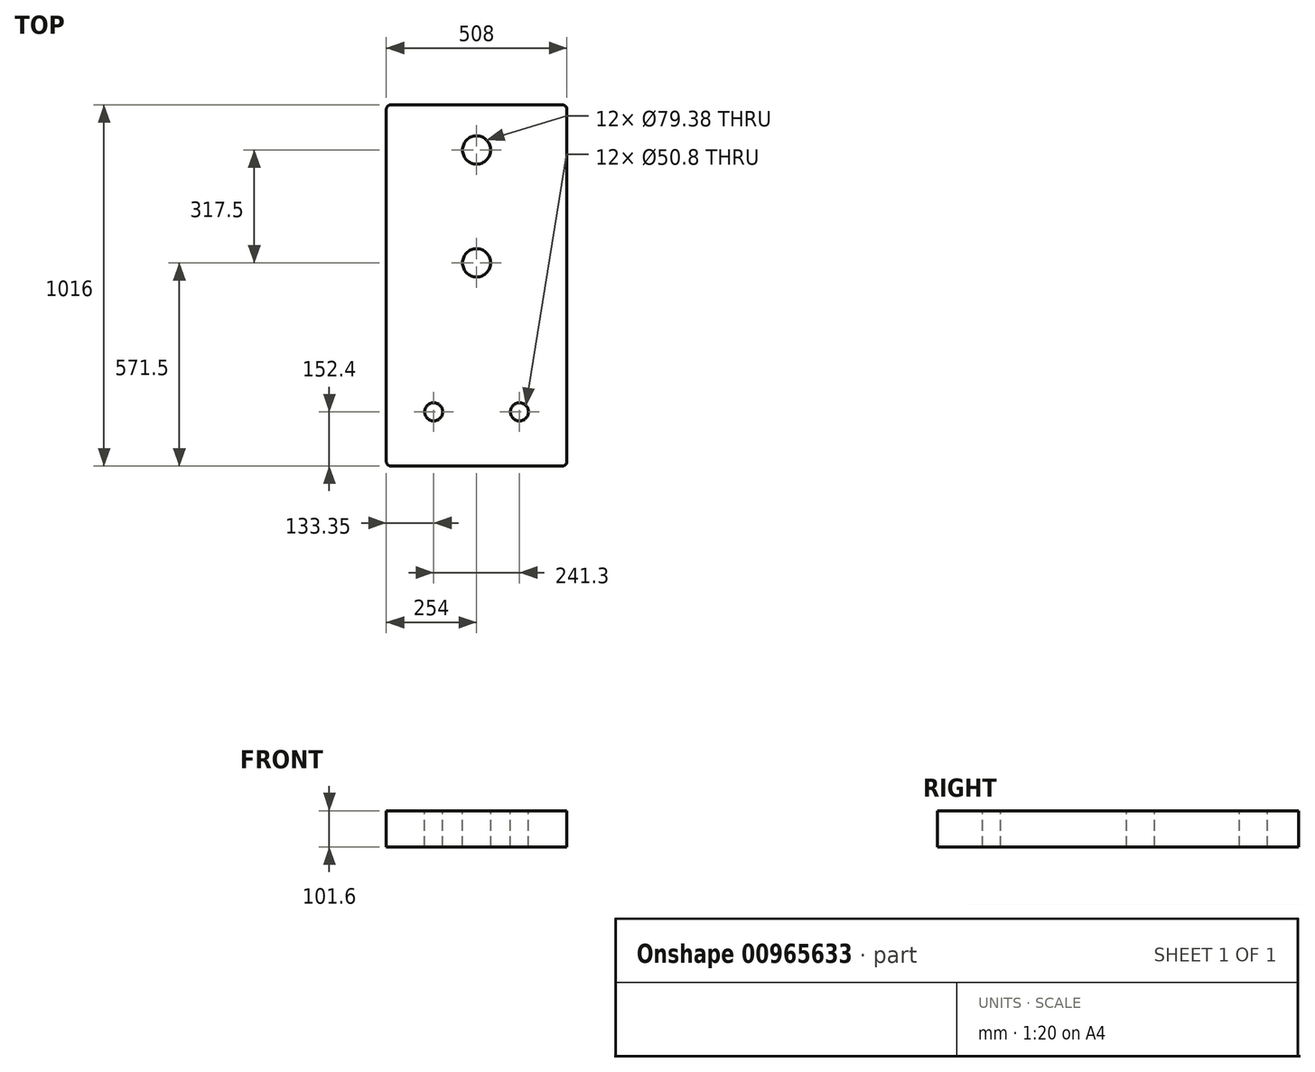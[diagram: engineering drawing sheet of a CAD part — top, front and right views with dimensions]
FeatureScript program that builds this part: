
annotation { "Feature Type Name" : "Feature", "Feature Type Description" : "" }
export const myFeature = defineFeature(function(context is Context, id is Id, definition is map)
    precondition{}
    {
        {
            var Q0;
            Q0=qCreatedBy(makeId("Top.planeOp"),FACE);
            var sketch = newSketch(context, id + "F0", { "sketchPlane" : qUnion([Q0])});
            skLineSegment(sketch, "E0.bottom", {"start": v(254, 508) * mm, "end": v(-254, 508) * mm});
            skLineSegment(sketch, "E0.top", {"start": v(254, -508) * mm, "end": v(-254, -508) * mm});
            skLineSegment(sketch, "E0.left", {"start": v(254, 508) * mm, "end": v(254, -508) * mm});
            skLineSegment(sketch, "E0.right", {"start": v(-254, 508) * mm, "end": v(-254, -508) * mm});
            skPoint(sketch, "E0.middle", {"position": v(0, 0) * mm});
            skSolve(sketch);
        }
        {
            var Q0;
            Q0=makeQuery(id+"F0.imprint","IMPRINT",FACE,{"disambiguationData":[TD([[makeQuery(id+"F0.imprint","IMPRINT",EDGE,{"derivedFrom":sQuery(id+"F0.wireOp",EDGE,"E0.bottom")}),1.0]])]});
            extrude(context, id + "F1", {"entities" : qUnion([Q0]), "depth" : 101.6 * mm, "offsetDistance" : 25.4 * mm});
        }
        {
            var Q0;
            Q0=makeQuery(id+"F1.opExtrude","CAP_FACE",FACE,{"disambiguationData":[OSD([sQuery(id+"F0.wireOp",EDGE,"E0.bottom"),sQuery(id+"F0.wireOp",EDGE,"E0.top"),sQuery(id+"F0.wireOp",EDGE,"E0.left"),sQuery(id+"F0.wireOp",EDGE,"E0.right")])],"isStart":false});
            var sketch = newSketch(context, id + "F2", { "sketchPlane" : qUnion([Q0])});
            skCircle(sketch, "E1", {"center": v(-120.65, -355.6) * mm, "radius": 25.4 * mm});
            skCircle(sketch, "E2", {"center": v(120.65, -355.6) * mm, "radius": 25.4 * mm});
            skLineSegment(sketch, "E3", {"start": v(-120.65, -355.6) * mm, "end": v(120.65, -355.6) * mm, "construction": true});
            skPoint(sketch, "E4", {"position": v(0, -355.6) * mm});
            skCircle(sketch, "E5", {"center": v(0, 63.5) * mm, "radius": 39.69 * mm});
            skLineSegment(sketch, "E6", {"start": v(0, 13.7) * mm, "end": v(0, 381) * mm, "construction": true});
            skCircle(sketch, "E7", {"center": v(0, 381) * mm, "radius": 39.69 * mm});
            skSolve(sketch);
        }
        {
            var Q0;
            Q0 = qSketchRegion(id + "F2", true);
            extrude(context, id + "F3", {"entities" : qUnion([Q0]), "operationType" : NewBodyOperationType.REMOVE, "endBound" : BoundingType.THROUGH_ALL, "oppositeDirection" : true, "depth" : 25.4 * mm, "offsetDistance" : 25.4 * mm});
        }
        {
            var Q0;
            Q0=makeQuery(id+"F1.opExtrude","SWEPT_EDGE",EDGE,{"disambiguationData":[OSD([sQuery(id+"F0.wireOp",EDGE,"E0.top"),sQuery(id+"F0.wireOp",EDGE,"E0.right")])]});
            var Q1;
            Q1=makeQuery(id+"F1.opExtrude","SWEPT_EDGE",EDGE,{"disambiguationData":[OSD([sQuery(id+"F0.wireOp",EDGE,"E0.top"),sQuery(id+"F0.wireOp",EDGE,"E0.left")])]});
            var Q2;
            Q2=makeQuery(id+"F1.opExtrude","SWEPT_EDGE",EDGE,{"disambiguationData":[OSD([sQuery(id+"F0.wireOp",EDGE,"E0.bottom"),sQuery(id+"F0.wireOp",EDGE,"E0.left")])]});
            var Q3;
            Q3=makeQuery(id+"F1.opExtrude","SWEPT_EDGE",EDGE,{"disambiguationData":[OSD([sQuery(id+"F0.wireOp",EDGE,"E0.bottom"),sQuery(id+"F0.wireOp",EDGE,"E0.right")])]});
            fillet(context, id + "F4", {"entities" : qUnion([Q0, Q1, Q2, Q3]), "radius" : 12.7 * mm, "tangentPropagation" : true, "allowEdgeOverflow" : false});
        }
    });
